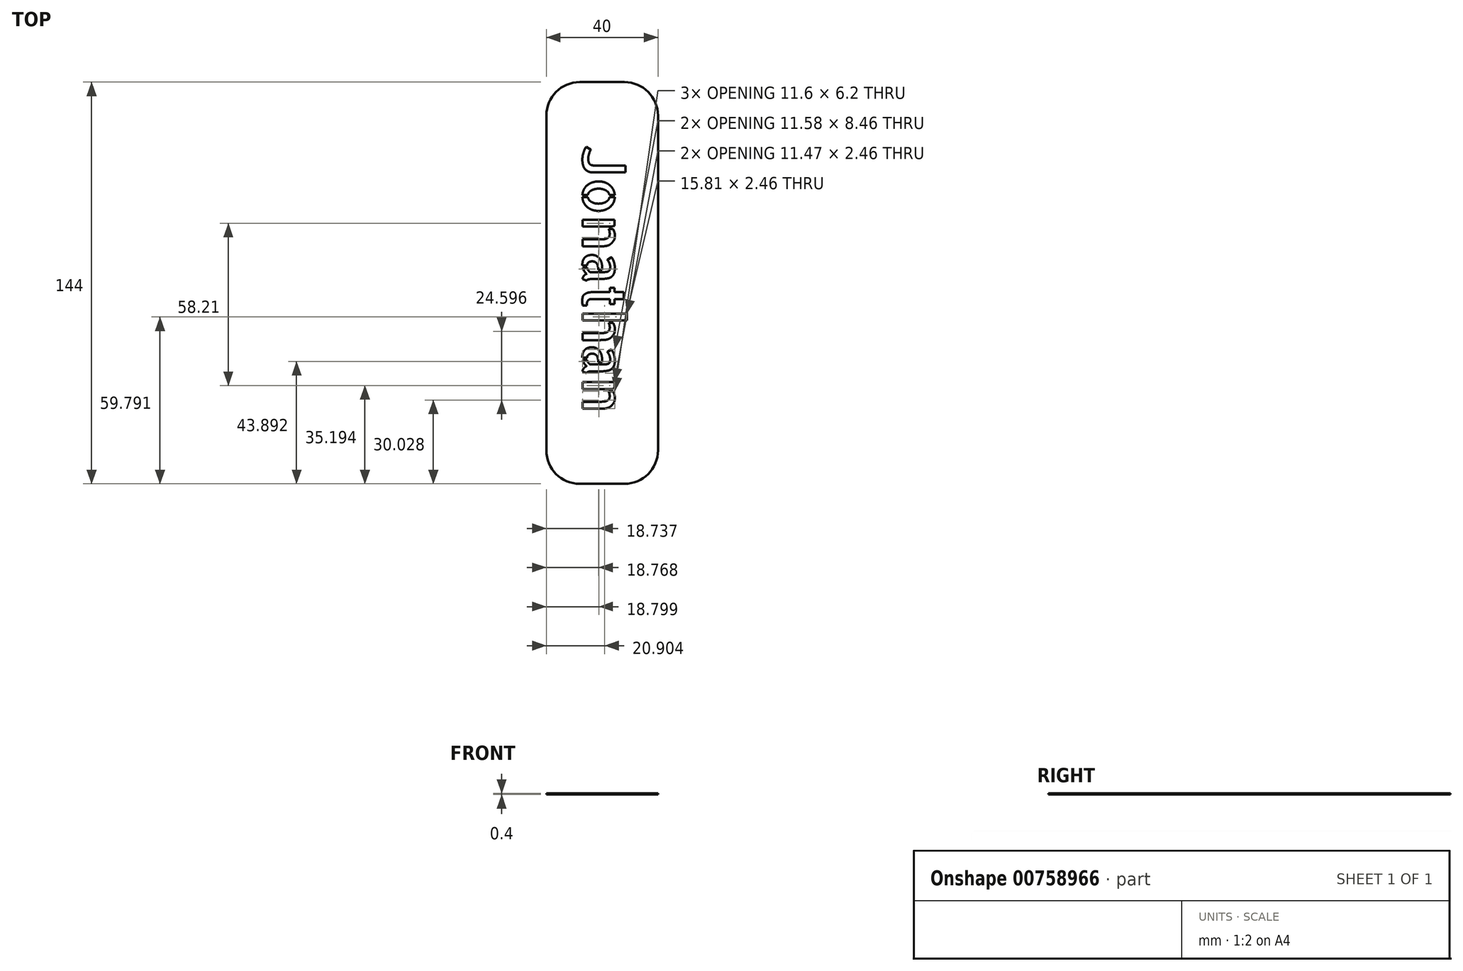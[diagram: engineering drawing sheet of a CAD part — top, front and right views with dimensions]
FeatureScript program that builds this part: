
annotation { "Feature Type Name" : "Feature", "Feature Type Description" : "" }
export const myFeature = defineFeature(function(context is Context, id is Id, definition is map)
    precondition{}
    {
        {
            var Q0;
            Q0=qCreatedBy(makeId("Top.planeOp"),FACE);
            var sketch = newSketch(context, id + "F0", { "sketchPlane" : qUnion([Q0])});
            skLineSegment(sketch, "E0.bottom", {"start": v(0, 0) * mm, "end": v(40, 0) * mm});
            skLineSegment(sketch, "E0.top", {"start": v(0, 144) * mm, "end": v(40, 144) * mm});
            skLineSegment(sketch, "E0.left", {"start": v(0, 0) * mm, "end": v(0, 144) * mm});
            skLineSegment(sketch, "E0.right", {"start": v(40, 0) * mm, "end": v(40, 144) * mm});
            skSolve(sketch);
        }
        {
            var Q0;
            Q0=makeQuery(id+"F0.imprint","IMPRINT",FACE,{"disambiguationData":[TD([[makeQuery(id+"F0.imprint","IMPRINT",EDGE,{"derivedFrom":sQuery(id+"F0.wireOp",EDGE,"E0.bottom")}),1.0]])]});
            extrude(context, id + "F1", {"entities" : qUnion([Q0]), "depth" : .4 * mm, "offsetDistance" : 25 * mm});
        }
        {
            var Q0;
            Q0=makeQuery(id+"F1.opExtrude","SWEPT_EDGE",EDGE,{"disambiguationData":[OSD([sQuery(id+"F0.wireOp",EDGE,"E0.top"),sQuery(id+"F0.wireOp",EDGE,"E0.left")])]});
            var Q1;
            Q1=makeQuery(id+"F1.opExtrude","SWEPT_EDGE",EDGE,{"disambiguationData":[OSD([sQuery(id+"F0.wireOp",EDGE,"E0.top"),sQuery(id+"F0.wireOp",EDGE,"E0.right")])]});
            var Q2;
            Q2=makeQuery(id+"F1.opExtrude","SWEPT_EDGE",EDGE,{"disambiguationData":[OSD([sQuery(id+"F0.wireOp",EDGE,"E0.bottom"),sQuery(id+"F0.wireOp",EDGE,"E0.right")])]});
            var Q3;
            Q3=makeQuery(id+"F1.opExtrude","SWEPT_EDGE",EDGE,{"disambiguationData":[OSD([sQuery(id+"F0.wireOp",EDGE,"E0.bottom"),sQuery(id+"F0.wireOp",EDGE,"E0.left")])]});
            fillet(context, id + "F2", {"entities" : qUnion([Q0, Q1, Q2, Q3]), "radius" : 12 * mm, "tangentPropagation" : true, "allowEdgeOverflow" : false});
        }
        {
            var Q0;
            Q0=makeQuery(id+"F1.opExtrude","CAP_FACE",FACE,{"disambiguationData":[OSD([sQuery(id+"F0.wireOp",EDGE,"E0.bottom"),sQuery(id+"F0.wireOp",EDGE,"E0.top"),sQuery(id+"F0.wireOp",EDGE,"E0.left"),sQuery(id+"F0.wireOp",EDGE,"E0.right")])],"isStart":false});
            var sketch = newSketch(context, id + "F3", { "sketchPlane" : qUnion([Q0])});
            skText(sketch, "E1", { "text": "Jonathan", "fontName": "AllertaStencil-Regular.ttf"});
            const initialGuessF3  = {"E1": [0.013, 0.12135, 0, -1, 0.015]};
            skSetInitialGuess(sketch, initialGuessF3);
            skSolve(sketch);
        }
        {
            var Q0;
            Q0=qSketchRegion(id+"F3",true);
            extrude(context, id + "F4", {"entities" : qUnion([Q0]), "operationType" : NewBodyOperationType.REMOVE, "endBound" : BoundingType.THROUGH_ALL, "oppositeDirection" : true, "depth" : 25 * mm, "offsetDistance" : 25 * mm});
        }
    });
